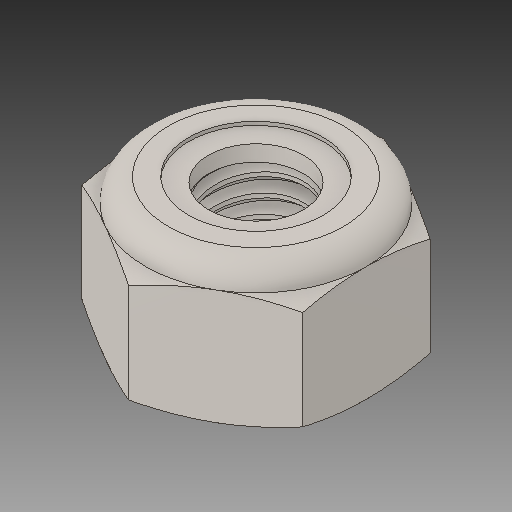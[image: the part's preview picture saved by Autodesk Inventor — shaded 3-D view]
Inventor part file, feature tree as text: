
AUTODESK INVENTOR PART (.ipt)
format: ipt  version: 2018 (Build 220112000, 112)  size: 318,464 bytes
history: native  units: in
note: dims shown in document units (in); Inventor stores cm internally (conversion verified against a paired STEP export)
features: other x1, revolve x1
ambient origin geometry x8: Origin, YZ Plane, XZ Plane, XY Plane, X Axis, Y Axis, Z Axis, Center Point
bodies: Solid1 (feature_tree), Solid2 (feature_tree)
feature tree (2):
  other  "Cut-Revolve4"
  revolve  "Revolve2"  [1 undecoded]
note: 1 required parameter value undecoded (feature->parameter linkage not recoverable at this tier; creation-order binding heuristic only, values carry confidence <= 0.55)
